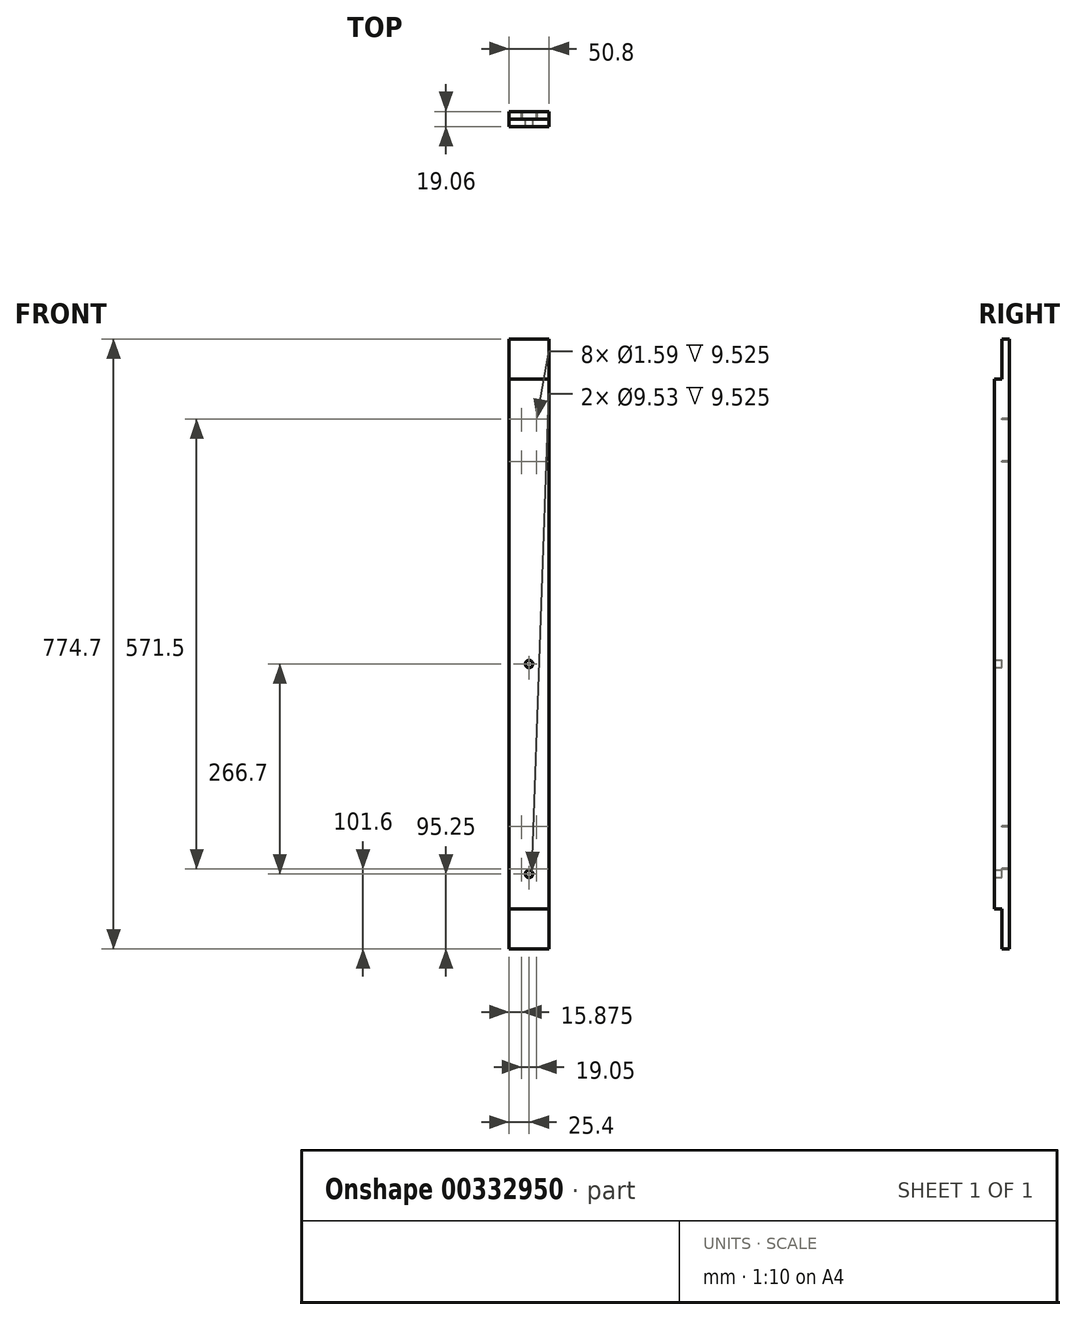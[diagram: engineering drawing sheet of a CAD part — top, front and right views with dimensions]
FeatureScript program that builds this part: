
annotation { "Feature Type Name" : "Feature", "Feature Type Description" : "" }
export const myFeature = defineFeature(function(context is Context, id is Id, definition is map)
    precondition{}
    {
        {
            var Q0;
            Q0=qCreatedBy(makeId("Top.planeOp"),FACE);
            var sketch = newSketch(context, id + "F0", { "sketchPlane" : qUnion([Q0])});
            skLineSegment(sketch, "E0.bottom", {"start": v(25.4, 9.53) * mm, "end": v(-25.4, 9.53) * mm});
            skLineSegment(sketch, "E0.top", {"start": v(25.4, -9.53) * mm, "end": v(-25.4, -9.53) * mm});
            skLineSegment(sketch, "E0.left", {"start": v(25.4, 9.53) * mm, "end": v(25.4, -9.52) * mm});
            skLineSegment(sketch, "E0.right", {"start": v(-25.4, 9.53) * mm, "end": v(-25.4, -9.53) * mm});
            skPoint(sketch, "E0.middle", {"position": v(0, 0) * mm});
            skSolve(sketch);
        }
        {
            var Q0;
            Q0=makeQuery(id+"F0.imprint","IMPRINT",FACE,{"disambiguationData":[TD([[makeQuery(id+"F0.imprint","IMPRINT",EDGE,{"derivedFrom":sQuery(id+"F0.wireOp",EDGE,"E0.bottom")}),1.0]])]});
            var Q1;
            Q1=qSketchRegion(id+"F2",true);
            extrude(context, id + "F1", {"entities" : qUnion([Q0, Q1]), "depth" : 774.7 * mm});
        }
        {
            var Q0;
            Q0=qCreatedBy(makeId("Front.planeOp"),FACE);
            var sketch = newSketch(context, id + "F2", { "sketchPlane" : qUnion([Q0])});
            skLineSegment(sketch, "E1.bottom", {"start": v(-38.77, 0) * mm, "end": v(83.66, 0) * mm});
            skLineSegment(sketch, "E1.top", {"start": v(-38.77, 50.8) * mm, "end": v(83.66, 50.8) * mm});
            skLineSegment(sketch, "E1.left", {"start": v(-38.77, 0) * mm, "end": v(-38.77, 50.8) * mm});
            skLineSegment(sketch, "E1.right", {"start": v(83.66, 0) * mm, "end": v(83.66, 50.8) * mm});
            skLineSegment(sketch, "E2.bottom", {"start": v(-210.36, 723.9) * mm, "end": v(132.8, 723.9) * mm});
            skLineSegment(sketch, "E2.top", {"start": v(-210.36, 774.7) * mm, "end": v(132.8, 774.7) * mm});
            skLineSegment(sketch, "E2.left", {"start": v(-210.36, 723.9) * mm, "end": v(-210.36, 774.7) * mm});
            skLineSegment(sketch, "E2.right", {"start": v(132.8, 723.9) * mm, "end": v(132.8, 774.7) * mm});
            skSolve(sketch);
        }
        {
            var Q0;
            Q0=qSketchRegion(id+"F2",true);
            extrude(context, id + "F3", {"entities" : qUnion([Q0]), "operationType" : NewBodyOperationType.REMOVE, "depth" : 25.4 * mm});
        }
        {
            var Q0;
            Q0=qCreatedBy(makeId("Front.planeOp"),FACE);
            var sketch = newSketch(context, id + "F4", { "sketchPlane" : qUnion([Q0])});
            skCircle(sketch, "E3", {"center": v(9.53, 101.6) * mm, "radius": 0.8 * mm});
            skCircle(sketch, "E4", {"center": v(9.52, 155.58) * mm, "radius": 0.8 * mm});
            skCircle(sketch, "E5", {"center": v(9.52, 619.12) * mm, "radius": 0.8 * mm});
            skCircle(sketch, "E6", {"center": v(9.52, 673.1) * mm, "radius": 0.8 * mm});
            skLineSegment(sketch, "E7", {"start": v(0, 0) * mm, "end": v(0, 1192.46) * mm, "construction": true});
            skLineSegment(sketch, "E8.bottom", {"start": v(9.52, 101.6) * mm, "end": v(-9.52, 101.6) * mm, "construction": true});
            skLineSegment(sketch, "E8.top", {"start": v(9.52, 673.1) * mm, "end": v(-9.53, 673.1) * mm, "construction": true});
            skLineSegment(sketch, "E8.left", {"start": v(9.53, 101.6) * mm, "end": v(9.52, 673.1) * mm, "construction": true});
            skLineSegment(sketch, "E8.right", {"start": v(-9.53, 101.6) * mm, "end": v(-9.53, 673.1) * mm, "construction": true});
            skCircle(sketch, "E9", {"center": v(-9.53, 619.12) * mm, "radius": 0.8 * mm});
            skCircle(sketch, "E10", {"center": v(-9.53, 673.1) * mm, "radius": 0.8 * mm});
            skCircle(sketch, "E11", {"center": v(-9.53, 101.6) * mm, "radius": 0.8 * mm});
            skCircle(sketch, "E12", {"center": v(-9.53, 155.58) * mm, "radius": 0.8 * mm});
            skSolve(sketch);
        }
        {
            var Q0;
            Q0=qSketchRegion(id+"F4",true);
            extrude(context, id + "F5", {"entities" : qUnion([Q0]), "operationType" : NewBodyOperationType.REMOVE, "oppositeDirection" : true, "depth" : 25.4 * mm});
        }
        {
            var Q0;
            Q0=qCreatedBy(makeId("Front.planeOp"),FACE);
            var sketch = newSketch(context, id + "F6", { "sketchPlane" : qUnion([Q0])});
            skCircle(sketch, "E13", {"center": v(0, 95.25) * mm, "radius": 4.76 * mm});
            skCircle(sketch, "E14", {"center": v(0, 361.95) * mm, "radius": 4.76 * mm});
            skSolve(sketch);
        }
        {
            var Q0;
            Q0=qSketchRegion(id+"F6",true);
            extrude(context, id + "F7", {"entities" : qUnion([Q0]), "operationType" : NewBodyOperationType.REMOVE, "depth" : 25.4 * mm});
        }
    });
